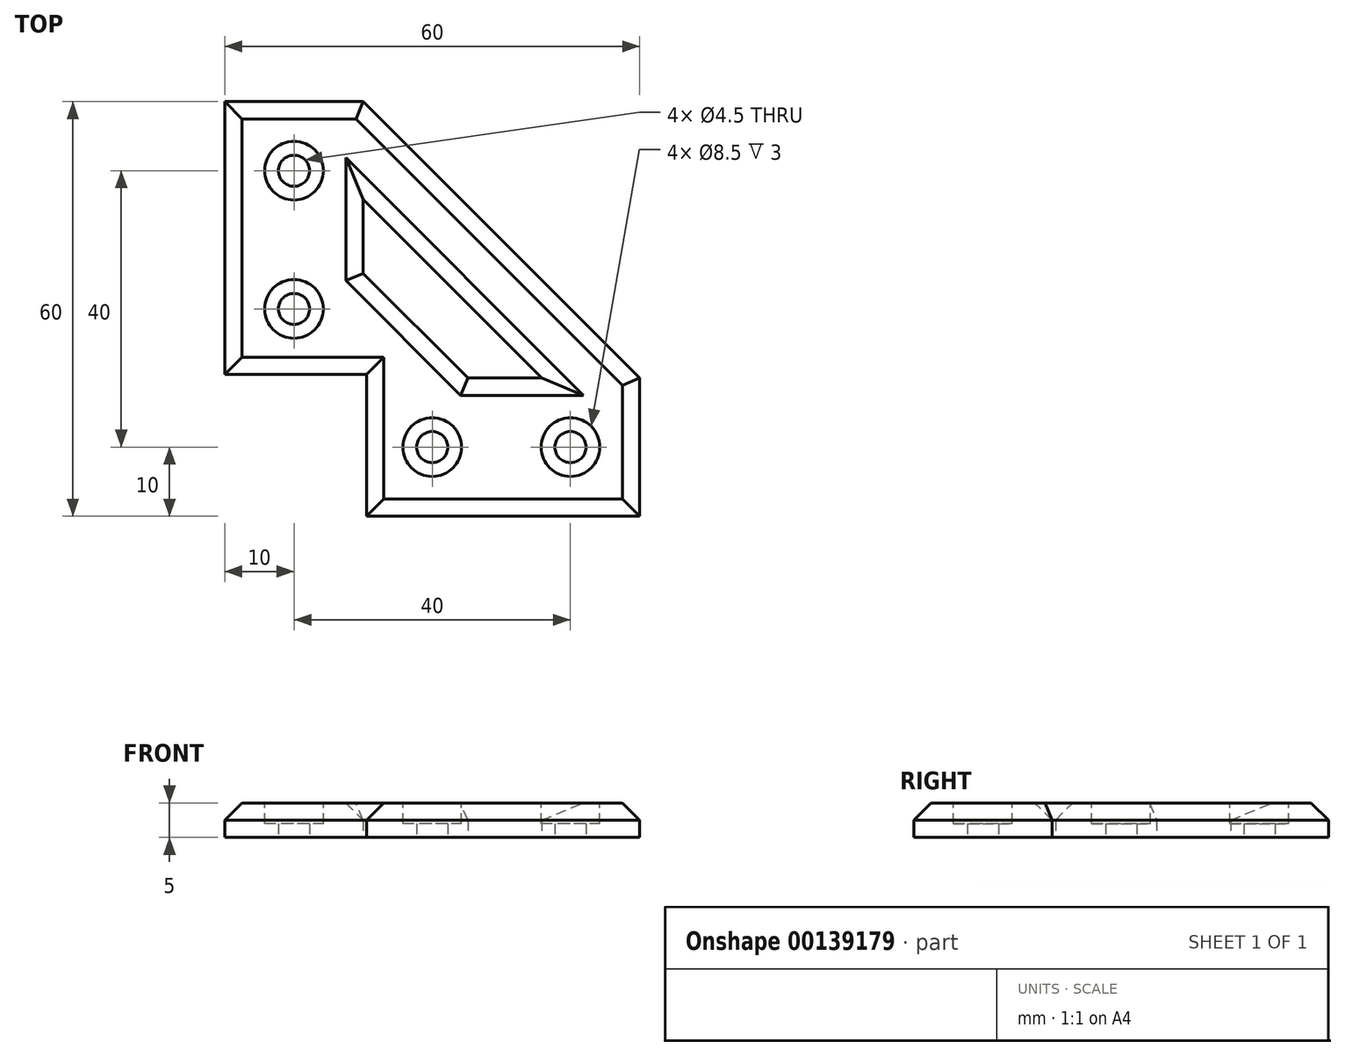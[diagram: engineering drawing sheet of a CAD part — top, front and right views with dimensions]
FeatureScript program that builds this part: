
annotation { "Feature Type Name" : "Feature", "Feature Type Description" : "" }
export const myFeature = defineFeature(function(context is Context, id is Id, definition is map)
    precondition{}
    {
        {
            var Q0;
            Q0=qCreatedBy(makeId("Top.planeOp"),FACE);
            var sketch = newSketch(context, id + "F0", { "sketchPlane" : qUnion([Q0])});
            skLineSegment(sketch, "E0", {"start": v(0, 20.5) * mm, "end": v(0, 60) * mm});
            skLineSegment(sketch, "E1", {"start": v(0, 60) * mm, "end": v(20, 60) * mm});
            skLineSegment(sketch, "E2", {"start": v(0, 20.5) * mm, "end": v(20.5, 20.5) * mm});
            skLineSegment(sketch, "E3", {"start": v(20.5, 20.5) * mm, "end": v(20.5, 0) * mm});
            skLineSegment(sketch, "E4", {"start": v(20.5, 0) * mm, "end": v(60, 0) * mm});
            skLineSegment(sketch, "E5", {"start": v(60, 0) * mm, "end": v(60, 20) * mm});
            skLineSegment(sketch, "E6", {"start": v(60, 20) * mm, "end": v(20, 60) * mm});
            skCircle(sketch, "E7", {"center": v(10, 50) * mm, "radius": 2.25 * mm});
            skPoint(sketch, "E7.centerSnap0", {"position": v(10, 60) * mm});
            skCircle(sketch, "E8", {"center": v(10, 30) * mm, "radius": 2.25 * mm});
            skLineSegment(sketch, "E9", {"start": v(20, 45.86) * mm, "end": v(45.86, 20) * mm});
            skLineSegment(sketch, "E10", {"start": v(20, 35.14) * mm, "end": v(35.14, 20) * mm});
            skLineSegment(sketch, "E11", {"start": v(35.14, 20) * mm, "end": v(45.86, 20) * mm});
            skLineSegment(sketch, "E12", {"start": v(20, 35.14) * mm, "end": v(20, 45.86) * mm});
            skLineSegment(sketch, "E13", {"start": v(0, 0) * mm, "end": v(20.5, 20.5) * mm});
            skCircle(sketch, "E14.MirrorC", {"center": v(30, 10) * mm, "radius": 2.25 * mm});
            skCircle(sketch, "E15.MirrorC", {"center": v(50, 10) * mm, "radius": 2.25 * mm});
            skSolve(sketch);
        }
        {
            var Q0;
            Q0=makeQuery(id+"F0.imprint","IMPRINT",FACE,{"disambiguationData":[TD([[makeQuery(id+"F0.imprint","IMPRINT",EDGE,{"derivedFrom":sQuery(id+"F0.wireOp",EDGE,"E0")}),-1.0]])]});
            extrude(context, id + "F1", {"entities" : qUnion([Q0]), "depth" : 5 * mm});
        }
        {
            var Q0;
            Q0=makeQuery(id+"F1.opExtrude","CAP_EDGE",EDGE,{"disambiguationData":[OSD([sQuery(id+"F0.wireOp",EDGE,"E2")])],"isStart":false});
            var Q1;
            Q1=makeQuery(id+"F1.opExtrude","CAP_EDGE",EDGE,{"disambiguationData":[OSD([sQuery(id+"F0.wireOp",EDGE,"E3")])],"isStart":false});
            var Q2;
            Q2=makeQuery(id+"F1.opExtrude","CAP_EDGE",EDGE,{"disambiguationData":[OSD([sQuery(id+"F0.wireOp",EDGE,"E4")])],"isStart":false});
            var Q3;
            Q3=makeQuery(id+"F1.opExtrude","CAP_EDGE",EDGE,{"disambiguationData":[OSD([sQuery(id+"F0.wireOp",EDGE,"E5")])],"isStart":false});
            var Q4;
            Q4=makeQuery(id+"F1.opExtrude","CAP_EDGE",EDGE,{"disambiguationData":[OSD([sQuery(id+"F0.wireOp",EDGE,"E6")])],"isStart":false});
            var Q5;
            Q5=makeQuery(id+"F1.opExtrude","CAP_EDGE",EDGE,{"disambiguationData":[OSD([sQuery(id+"F0.wireOp",EDGE,"E1")])],"isStart":false});
            var Q6;
            Q6=makeQuery(id+"F1.opExtrude","CAP_EDGE",EDGE,{"disambiguationData":[OSD([sQuery(id+"F0.wireOp",EDGE,"E0")])],"isStart":false});
            var Q7;
            Q7=makeQuery(id+"F1.opExtrude","CAP_EDGE",EDGE,{"disambiguationData":[OSD([sQuery(id+"F0.wireOp",EDGE,"E12")])],"isStart":false});
            var Q8;
            Q8=makeQuery(id+"F1.opExtrude","CAP_EDGE",EDGE,{"disambiguationData":[OSD([sQuery(id+"F0.wireOp",EDGE,"E9")])],"isStart":false});
            var Q9;
            Q9=makeQuery(id+"F1.opExtrude","CAP_EDGE",EDGE,{"disambiguationData":[OSD([sQuery(id+"F0.wireOp",EDGE,"E11")])],"isStart":false});
            var Q10;
            Q10=makeQuery(id+"F1.opExtrude","CAP_EDGE",EDGE,{"disambiguationData":[OSD([sQuery(id+"F0.wireOp",EDGE,"E10")])],"isStart":false});
            chamfer(context, id + "F2", {"entities" : qUnion([Q0, Q1, Q2, Q3, Q4, Q5, Q6, Q7, Q8, Q9, Q10]), "width" : 2.5 * mm, "tangentPropagation" : true});
        }
        {
            var Q0;
            Q0=makeQuery(id+"F1.opExtrude","CAP_FACE",FACE,{"disambiguationData":[OSD([sQuery(id+"F0.wireOp",EDGE,"E0"),sQuery(id+"F0.wireOp",EDGE,"E1"),sQuery(id+"F0.wireOp",EDGE,"E2"),sQuery(id+"F0.wireOp",EDGE,"E3"),sQuery(id+"F0.wireOp",EDGE,"E4"),sQuery(id+"F0.wireOp",EDGE,"E5"),sQuery(id+"F0.wireOp",EDGE,"E6"),sQuery(id+"F0.wireOp",EDGE,"E7"),sQuery(id+"F0.wireOp",EDGE,"E8"),sQuery(id+"F0.wireOp",EDGE,"E9"),sQuery(id+"F0.wireOp",EDGE,"E10"),sQuery(id+"F0.wireOp",EDGE,"E11"),sQuery(id+"F0.wireOp",EDGE,"E12"),sQuery(id+"F0.wireOp",EDGE,"E14.MirrorC"),sQuery(id+"F0.wireOp",EDGE,"E15.MirrorC")])],"isStart":false});
            var sketch = newSketch(context, id + "F3", { "sketchPlane" : qUnion([Q0])});
            skCircle(sketch, "E16", {"center": v(10, 50) * mm, "radius": 4.25 * mm});
            skCircle(sketch, "E17", {"center": v(10, 30) * mm, "radius": 4.25 * mm});
            skCircle(sketch, "E18", {"center": v(30, 10) * mm, "radius": 4.25 * mm});
            skCircle(sketch, "E19", {"center": v(50, 10) * mm, "radius": 4.25 * mm});
            skSolve(sketch);
        }
        {
            var Q0;
            Q0=makeQuery(id+"F3.imprint","IMPRINT",FACE,{"disambiguationData":[TD([[makeQuery(id+"F3.imprint","IMPRINT",EDGE,{"derivedFrom":sQuery(id+"F3.wireOp",EDGE,"E16")}),1.0]])]});
            var Q1;
            Q1=makeQuery(id+"F3.imprint","IMPRINT",FACE,{"disambiguationData":[TD([[makeQuery(id+"F3.imprint","IMPRINT",EDGE,{"derivedFrom":sQuery(id+"F3.wireOp",EDGE,"E17")}),1.0]])]});
            var Q2;
            Q2=makeQuery(id+"F3.imprint","IMPRINT",FACE,{"disambiguationData":[TD([[makeQuery(id+"F3.imprint","IMPRINT",EDGE,{"derivedFrom":sQuery(id+"F3.wireOp",EDGE,"E18")}),1.0]])]});
            var Q3;
            Q3=makeQuery(id+"F3.imprint","IMPRINT",FACE,{"disambiguationData":[TD([[makeQuery(id+"F3.imprint","IMPRINT",EDGE,{"derivedFrom":sQuery(id+"F3.wireOp",EDGE,"E19")}),1.0]])]});
            extrude(context, id + "F4", {"entities" : qUnion([Q0, Q1, Q2, Q3]), "operationType" : NewBodyOperationType.REMOVE, "oppositeDirection" : true, "depth" : 3 * mm});
        }
    });
